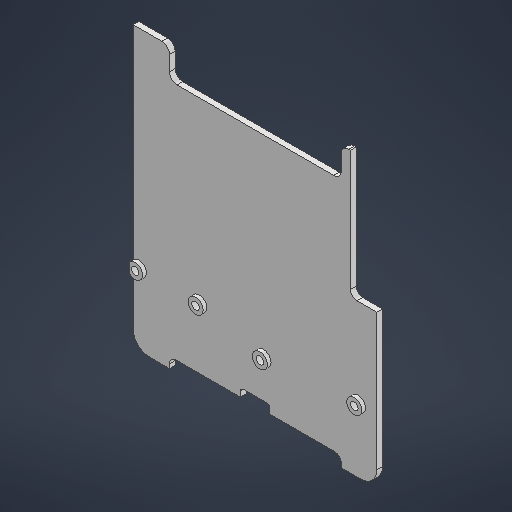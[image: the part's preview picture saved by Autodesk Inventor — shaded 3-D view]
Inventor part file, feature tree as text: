
AUTODESK INVENTOR PART (.ipt)
format: ipt  version: 2025 (Build 290162000, 162)  size: 322,560 bytes
history: native  units: mm
features: extrude x7, sketch x7, projected_geometry x5, fillet x3, other x3, reference x1
ambient origin geometry x8: Origin, YZ Plane, XZ Plane, XY Plane, X Axis, Y Axis, Z Axis, Center Point
bodies: 实体1 (feature_tree)
feature tree (26):
  extrude  "拉伸1"  Depth=1.5mm
  extrude  "拉伸2"  Depth=1.0mm
  fillet  "圆角1"  Radius=10.0mm
  extrude  "拉伸3"  Depth=7.0mm
  fillet  "圆角2"  Radius=32.0mm
  extrude  "拉伸4"  Depth=10.0mm TaperAngle=0.0deg
  extrude  "拉伸5"  Depth=2.0mm
  fillet  "圆角3"  Radius=1.0mm
  extrude  "拉伸7"  Depth=1.0mm
  extrude  "拉伸8"  Depth=1.0mm TaperAngle=0.0deg
  sketch  "草图1"  dims[d0=1.5mm d1=0.0mm d3=3.0mm]
  sketch  "草图2"  dims[d4=2.0mm d5=0.0mm d6=1.0mm d7=10.0mm d8=0.0mm]
  sketch  "草图3"  dims[d9=1.0mm d10=7.0mm d11=32.0mm]
  reference  "参考2"
  sketch  "草图4"  dims[d12=10.0mm d13=0.0mm d14=10.0mm d15=0.0mm]
  projected_geometry  "投影回路1"
  sketch  "草图5"  dims[d16=8.0mm d17=2.0mm d20=1.0mm]
  sketch  "草图6"  dims[d21=1.0mm d22=1.0mm]
  sketch  "草图7"  dims[d23=1.0mm d24=1.0mm d25=0.0mm d26=7.0mm d27=0.0mm d28=25.0mm d29=17.0mm d30=16.0mm d33=12.008404mm d35=5.0mm d36=2.0mm d37=4.0mm]
  projected_geometry  "投影回路2"
  projected_geometry  "投影回路3"
  projected_geometry  "投影回路4"
  projected_geometry  "投影回路5"
  parser-record x1  (decoder bookkeeping rows leaked as tree rows — omitted from the tree; the rows remain in map.json)
  other  "装配体.iam"
  other  "键盘外壳:1"
note: 1 file-system path scrubbed to <path> (originals preserved in map.json)
